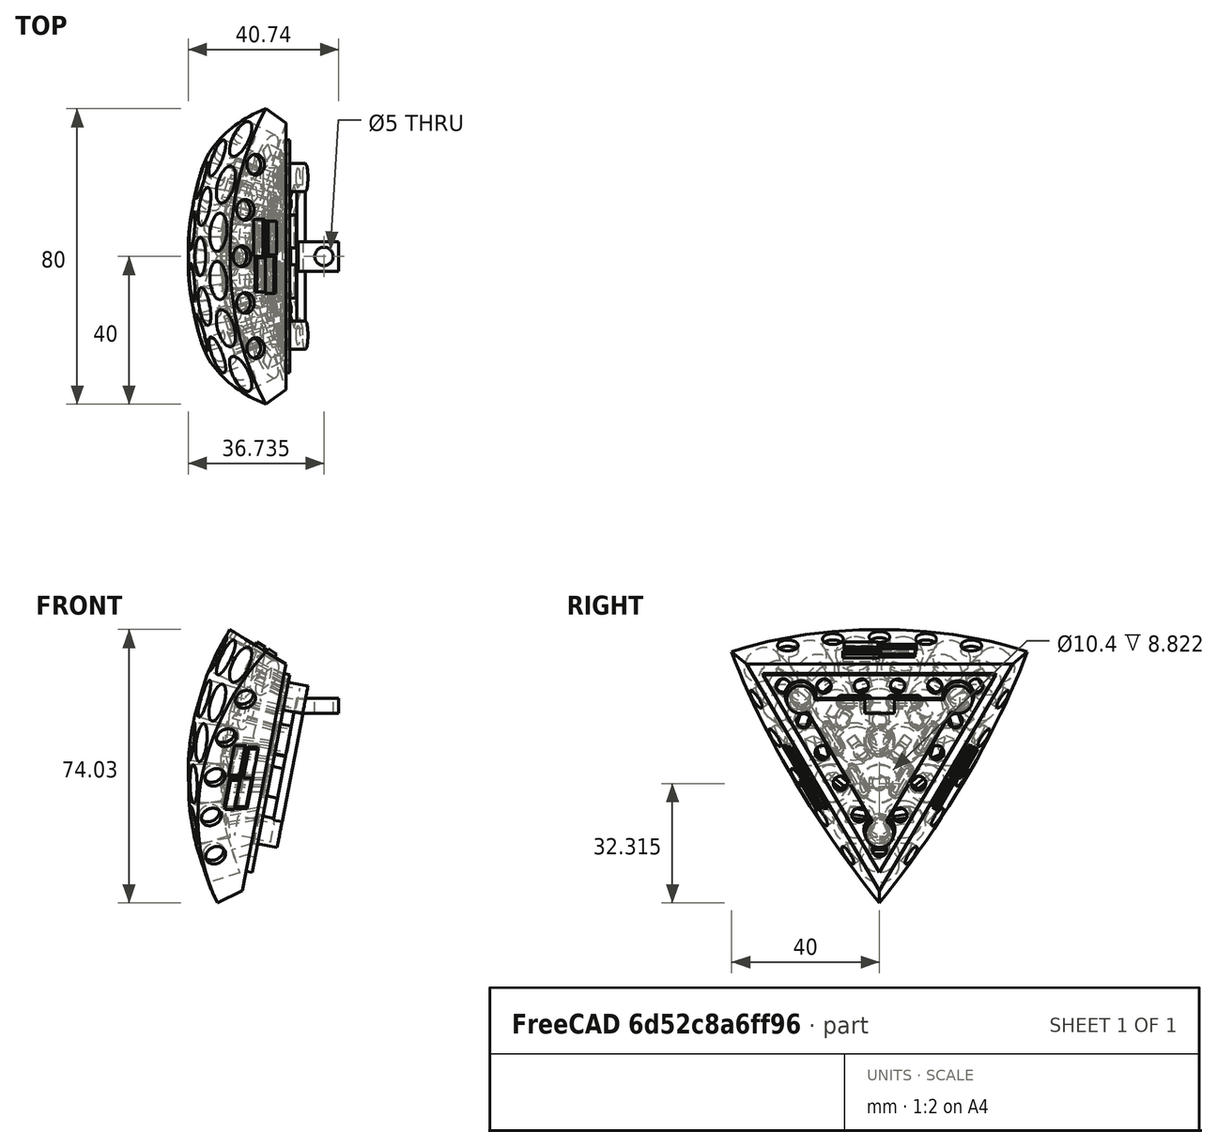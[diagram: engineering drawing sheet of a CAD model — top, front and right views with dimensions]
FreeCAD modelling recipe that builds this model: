
FCSTD DOCUMENT  (FreeCAD 0.20R27422 (Git))
Label: Inner_rev2
License: All rights reserved
LicenseURL: http://en.wikipedia.org/wiki/All_rights_reserved
objects: PartDesign::Line×25, Part::Feature×5, App::Part×5, Part::Chamfer×4, Part::Part2DObjectPython×1, PartDesign::CoordinateSystem×1
note: 36 computed .brp shape members not serialized (recipe doc carries the construction recipe); baked Part::Feature solids carry a one-line shape summary decoded from their .brp

FEATURE [Part::Part2DObjectPython] Line  # Draft 2D object (typed FeaturePython)
  Area = 0
  ChamferSize = 0
  Closed = false
  End = (-60.4609,0,-2.48e-14)
  FilletRadius = 0
  Length = 60.4609
  MakeFace = true
  Points = (2) [(0,0,0),(-60.4609,0,-2.4803e-14)]
  Start = (0,0,0)
  Subdivisions = 0
FEATURE [Part::Feature] Shape  label="shell"
  Placement = pos=(0,0,0) rot=(0,1,0;0.188711rad)
  shape: bbox 26.49 x 83.96 x 75.99 mm, 229 faces (baked)
FEATURE [Part::Feature] Shape001  label="pcb"
  Placement = pos=(0,0,0) rot=(0,1,0;0.188711rad)
  shape: bbox 11.8 x 62.95 x 53.85 mm, 64 faces (baked)
FEATURE [Part::Feature] Shape002
  shape: bbox 23.55 x 50.22 x 45.04 mm, 88 faces (baked)
FEATURE [Part::Feature] Shape003
  shape: bbox 23.55 x 50.22 x 45.04 mm, 88 faces (baked)
FEATURE [Part::Feature] Shape004
  shape: bbox 23.55 x 50.22 x 45.04 mm, 88 faces (baked)
FEATURE [Part::Chamfer] Chamfer
  Base = -> Shape002
  Edges = 6 edges r=0.7: [Edge84,Edge94,Edge102,Edge112,Edge122,Edge128]
FEATURE [Part::Chamfer] Chamfer001  label="inner_center_rev2"
  Base = -> Chamfer
  Edges = 4 edges r=0.7: [Edge57,Edge71,Edge76,Edge118]
FEATURE [Part::Chamfer] Chamfer002  label="inner_right_rev2"
  Base = -> Shape004
  Edges = 10 edges r=0.7: [Edge69,Edge71,Edge75,Edge88,Edge89,Edge102,Edge112,Edge114,Edge122,Edge128]
FEATURE [Part::Chamfer] Chamfer003  label="inner_left_rev2"
  Base = -> Shape003
  Edges = 10 edges r=0.7: [Edge69,Edge71,Edge75,Edge84,Edge94,Edge102,Edge105,Edge114,Edge122,Edge126]
FEATURE [App::Part] Part004  label="pcb_part"
  Group = -> [Shape001]
  Origin = -> Origin004
FEATURE [PartDesign::Line] HoleAxis_1  label="top_center_magnet_axis"
  AttacherType = Attacher::AttachEngineLine
  Length = 7.89078
  MapMode = 19
  Placement = pos=(-61.4889,0,38.0022) rot=(0,1,0;3.69517rad)
  ResizeMode = 1
  Support = -> [Shape]
FEATURE [PartDesign::Line] HoleAxis_2  label="left_center_magnet_axis"
  AttacherType = Attacher::AttachEngineLine
  Length = 7.8873
  MapMode = 19
  Placement = pos=(-68.7467,-22.3371,-8.2e-15) rot=(-0.076899,0.485523,0.870835;3.41572rad)
  ResizeMode = 1
  Support = -> [Shape]
FEATURE [PartDesign::Line] HoleAxis_3  label="right_center_magnet_axis"
  AttacherType = Attacher::AttachEngineLine
  Length = 7.8873
  MapMode = 19
  Placement = pos=(-68.7467,22.3371,-2.74e-14) rot=(-0.076899,-0.485523,0.870835;2.86747rad)
  ResizeMode = 1
  Support = -> [Shape]
FEATURE [PartDesign::Line] HoleAxis_4  label="top_left_magnet_axis"
  AttacherType = Attacher::AttachEngineLine
  Length = 7.89078
  MapMode = 19
  Placement = pos=(-57.7484,-24.8267,35.6905) rot=(0,1,0;3.69517rad)
  ResizeMode = 1
  Support = -> [Shape]
FEATURE [PartDesign::Line] HoleAxis_5  label="left_right_magnet_axis"
  AttacherType = Attacher::AttachEngineLine
  Length = 7.8873
  MapMode = 19
  Placement = pos=(-68.598,-8.56496,-21.1189) rot=(-0.076899,0.485523,0.870835;3.41572rad)
  ResizeMode = 1
  Support = -> [Shape]
FEATURE [PartDesign::Line] HoleAxis_6  label="right_top_magnet_axis"
  AttacherType = Attacher::AttachEngineLine
  Length = 7.8873
  MapMode = 19
  Placement = pos=(-60.5313,33.3917,21.1189) rot=(-0.076899,-0.485523,0.870835;2.86747rad)
  ResizeMode = 1
  Support = -> [Shape]
FEATURE [PartDesign::Line] HoleAxis_7  label="flat_top_left_magnet_axis"
  AttacherType = Attacher::AttachEngineLine
  Length = 7.32715
  MapMode = 19
  Placement = pos=(-51.1858,-21.3123,22.3027) rot=(0,-1,0;1.38209rad)
  ResizeMode = 1
  Support = -> [Shape]
FEATURE [PartDesign::Line] HoleAxis_8  label="flat_top_right_magnet_axis"
  AttacherType = Attacher::AttachEngineLine
  Length = 7.32715
  MapMode = 19
  Placement = pos=(-51.1858,21.3123,22.3027) rot=(0,-1,0;1.38209rad)
  ResizeMode = 1
  Support = -> [Shape]
FEATURE [PartDesign::Line] HoleAxis_9  label="flat_bottom_magnet_axis"
  AttacherType = Attacher::AttachEngineLine
  Length = 7.32715
  MapMode = 19
  Placement = pos=(-58.1106,-1.2e-14,-13.956) rot=(0,-1,0;1.38209rad)
  ResizeMode = 1
  Support = -> [Shape]
FEATURE [PartDesign::Line] HoleAxis_10  label="flat_center_magnet_axis"
  AttacherType = Attacher::AttachEngineLine
  Length = 7.32715
  MapMode = 19
  Placement = pos=(-53.4941,-5e-15,10.2165) rot=(0,-1,0;1.38209rad)
  ResizeMode = 1
  Support = -> [Shape]
FEATURE [PartDesign::CoordinateSystem] LCS_1  label="flat_center_lcs"
  AttacherType = Attacher::AttachEngine3D
  MapMode = 11
  Placement = pos=(-53.4941,-5e-15,10.2165) rot=(-0.537462,-0.537462,0.649822;1.98909rad)
  Support = -> [Shape]
FEATURE [App::Part] Part  label="shell_part"
  Group = -> [Shape,HoleAxis_1,HoleAxis_2,HoleAxis_3,HoleAxis_4,HoleAxis_5,HoleAxis_6,HoleAxis_7,HoleAxis_8,HoleAxis_9,HoleAxis_10,LCS_1]
  Origin = -> Origin
FEATURE [PartDesign::Line] HoleAxis_11  label="screw_axis"
  AttacherType = Attacher::AttachEngineLine
  Length = 7.04534
  MapMode = 19
  Placement = pos=(-39.2746,0,21.3647) rot=(0,0,1;0rad)
  ResizeMode = 1
  Support = -> [Chamfer001]
FEATURE [PartDesign::Line] HoleAxis_12  label="left_top_axis"
  AttacherType = Attacher::AttachEngineLine
  Length = 7.32715
  MapMode = 19
  Placement = pos=(-51.1858,21.3123,22.3027) rot=(0,1,0;1.75951rad)
  ResizeMode = 1
  Support = -> [Chamfer001]
FEATURE [PartDesign::Line] HoleAxis_13  label="right_top_axis"
  AttacherType = Attacher::AttachEngineLine
  Length = 7.32715
  MapMode = 19
  Placement = pos=(-51.1858,-21.3123,22.3027) rot=(0,1,0;1.75951rad)
  ResizeMode = 1
  Support = -> [Chamfer001]
FEATURE [PartDesign::Line] HoleAxis_14  label="bottom_axis"
  AttacherType = Attacher::AttachEngineLine
  Length = 7.32715
  MapMode = 19
  Placement = pos=(-58.1106,-1.2e-14,-13.956) rot=(0,1,0;1.75951rad)
  ResizeMode = 1
  Support = -> [Chamfer001]
FEATURE [PartDesign::Line] HoleAxis_15  label="center_axis"
  AttacherType = Attacher::AttachEngineLine
  Length = 7.32715
  MapMode = 19
  Placement = pos=(-53.4941,-5e-15,10.2165) rot=(0,1,0;1.75951rad)
  ResizeMode = 1
  Support = -> [Chamfer001]
FEATURE [App::Part] Part001  label="inner_center_part"
  Group = -> [Shape002,Chamfer,Chamfer001,HoleAxis_11,HoleAxis_12,HoleAxis_13,HoleAxis_14,HoleAxis_15]
  Origin = -> Origin001
FEATURE [PartDesign::Line] HoleAxis_16  label="screw_axis001"
  AttacherType = Attacher::AttachEngineLine
  Length = 7.04534
  MapMode = 19
  Placement = pos=(-39.2746,-12.7874,21.3647) rot=(0,0,1;0rad)
  ResizeMode = 1
  Support = -> [Chamfer003]
FEATURE [PartDesign::Line] HoleAxis_17  label="left_top_axis001"
  AttacherType = Attacher::AttachEngineLine
  Length = 7.32715
  MapMode = 19
  Placement = pos=(-51.1858,21.3123,22.3027) rot=(0,1,0;1.75951rad)
  ResizeMode = 1
  Support = -> [Chamfer003]
FEATURE [PartDesign::Line] HoleAxis_18  label="right_top_axis001"
  AttacherType = Attacher::AttachEngineLine
  Length = 7.32715
  MapMode = 19
  Placement = pos=(-51.1858,-21.3123,22.3027) rot=(0,1,0;1.75951rad)
  ResizeMode = 1
  Support = -> [Chamfer003]
FEATURE [PartDesign::Line] HoleAxis_19  label="center_axis001"
  AttacherType = Attacher::AttachEngineLine
  Length = 7.32715
  MapMode = 19
  Placement = pos=(-53.4941,-5e-15,10.2165) rot=(0,1,0;1.75951rad)
  ResizeMode = 1
  Support = -> [Chamfer003]
FEATURE [PartDesign::Line] HoleAxis_20  label="bottom_axis001"
  AttacherType = Attacher::AttachEngineLine
  Length = 7.32715
  MapMode = 19
  Placement = pos=(-58.1106,-1.2e-14,-13.956) rot=(0,1,0;1.75951rad)
  ResizeMode = 1
  Support = -> [Chamfer003]
FEATURE [App::Part] Part002  label="inner_left_part"
  Group = -> [Shape003,Chamfer003,HoleAxis_16,HoleAxis_17,HoleAxis_18,HoleAxis_19,HoleAxis_20]
  Origin = -> Origin002
FEATURE [PartDesign::Line] HoleAxis_21  label="screw_axis002"
  AttacherType = Attacher::AttachEngineLine
  Length = 7.04534
  MapMode = 19
  Placement = pos=(-39.2746,12.7874,21.3647) rot=(0,0,1;0rad)
  ResizeMode = 1
  Support = -> [Chamfer002]
FEATURE [PartDesign::Line] HoleAxis_22  label="left_top_axis002"
  AttacherType = Attacher::AttachEngineLine
  Length = 7.32715
  MapMode = 19
  Placement = pos=(-51.1858,21.3123,22.3027) rot=(0,1,0;1.75951rad)
  ResizeMode = 1
  Support = -> [Chamfer002]
FEATURE [PartDesign::Line] HoleAxis_23  label="right_top_axis002"
  AttacherType = Attacher::AttachEngineLine
  Length = 7.32715
  MapMode = 19
  Placement = pos=(-51.1858,-21.3123,22.3027) rot=(0,1,0;1.75951rad)
  ResizeMode = 1
  Support = -> [Chamfer002]
FEATURE [PartDesign::Line] HoleAxis_24  label="center_axis002"
  AttacherType = Attacher::AttachEngineLine
  Length = 7.32715
  MapMode = 19
  Placement = pos=(-53.4941,-5e-15,10.2165) rot=(0,1,0;1.75951rad)
  ResizeMode = 1
  Support = -> [Chamfer002]
FEATURE [PartDesign::Line] HoleAxis_25  label="bottom_axis002"
  AttacherType = Attacher::AttachEngineLine
  Length = 7.32715
  MapMode = 19
  Placement = pos=(-58.1106,-1.2e-14,-13.956) rot=(0,1,0;1.75951rad)
  ResizeMode = 1
  Support = -> [Chamfer002]
FEATURE [App::Part] Part003  label="inner_right_part"
  Group = -> [Shape004,Chamfer002,HoleAxis_21,HoleAxis_22,HoleAxis_23,HoleAxis_24,HoleAxis_25]
  Origin = -> Origin003
